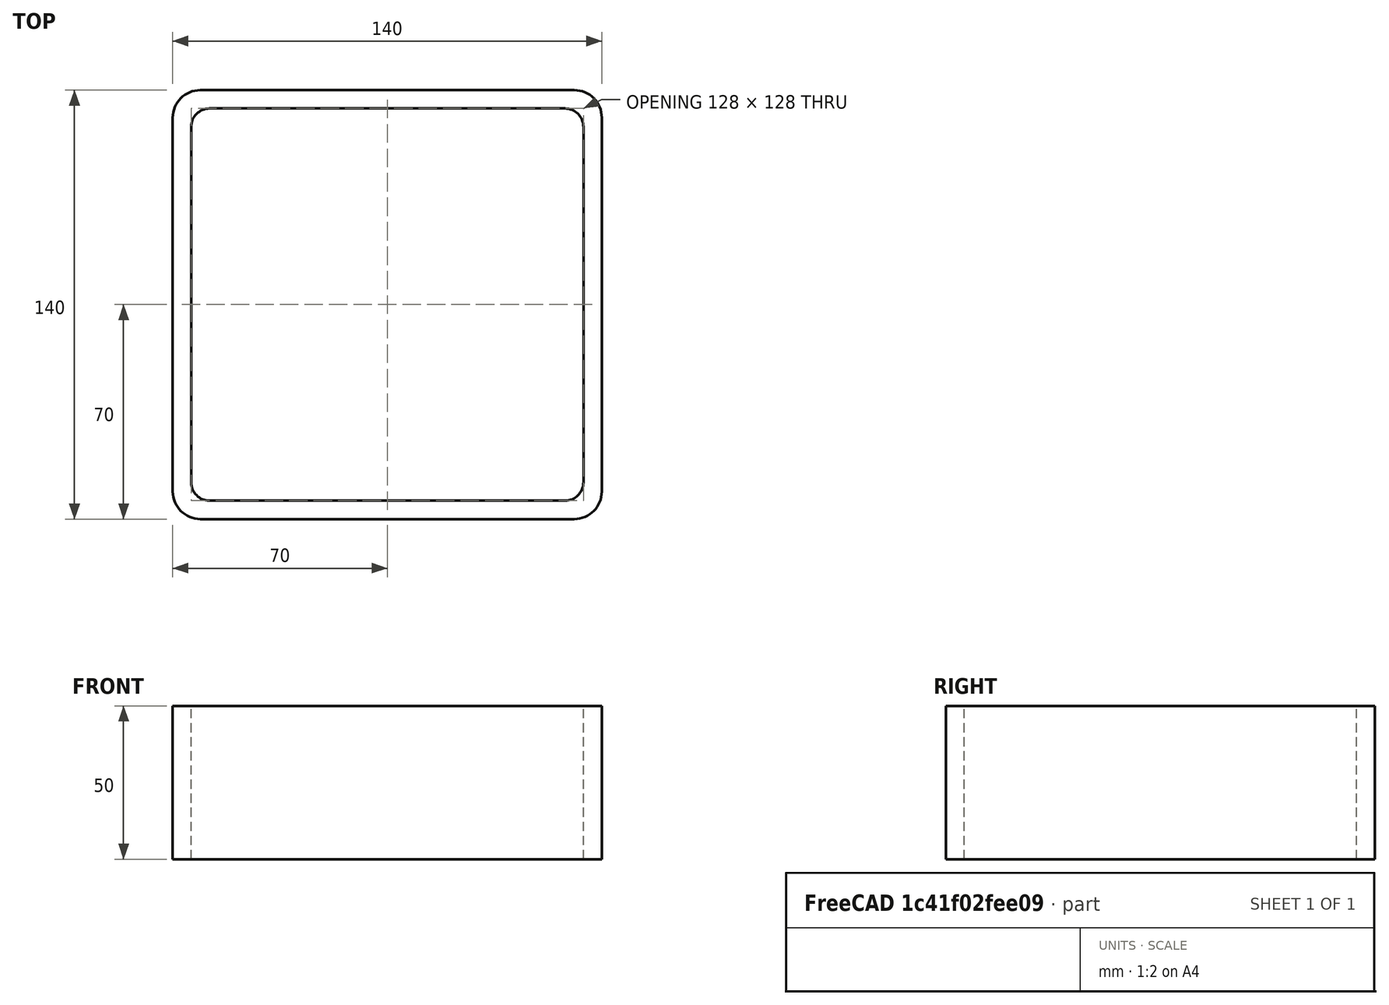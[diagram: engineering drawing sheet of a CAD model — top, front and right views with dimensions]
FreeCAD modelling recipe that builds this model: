
FCSTD DOCUMENT  (FreeCAD 0.15R4671 (Git))
Label: Square hollow section 140x140x6 EN10219 S235JRH
License: All rights reserved
LicenseURL: http://en.wikipedia.org/wiki/All_rights_reserved
objects: Sketcher::SketchObject×1, Part::Extrusion×1
note: 2 computed .brp shape members not serialized (recipe doc carries the construction recipe); baked Part::Feature solids carry a one-line shape summary decoded from their .brp

FEATURE [Sketcher::SketchObject] Sketch
  sketch-geometry (16):
    g0: LineSegment StartX=-58 StartY=64 StartZ=0 EndX=58 EndY=64 EndZ=0
    g1: LineSegment StartX=64 StartY=58 StartZ=0 EndX=64 EndY=-58 EndZ=0
    g2: LineSegment StartX=58 StartY=-64 StartZ=0 EndX=-58 EndY=-64 EndZ=0
    g3: LineSegment StartX=-64 StartY=-58 StartZ=0 EndX=-64 EndY=58 EndZ=0
    g4: LineSegment StartX=-61 StartY=70 StartZ=0 EndX=61 EndY=70 EndZ=0
    g5: LineSegment StartX=70 StartY=61 StartZ=0 EndX=70 EndY=-61 EndZ=0
    g6: LineSegment StartX=61 StartY=-70 StartZ=0 EndX=-61 EndY=-70 EndZ=0
    g7: LineSegment StartX=-70 StartY=-61 StartZ=0 EndX=-70 EndY=61 EndZ=0
    g8: ArcOfCircle CenterX=-58 CenterY=58 CenterZ=0 NormalX=0 NormalY=0 NormalZ=1 Radius=6 StartAngle=1.5708 EndAngle=3.14159
    g9: ArcOfCircle CenterX=58 CenterY=58 CenterZ=0 NormalX=0 NormalY=0 NormalZ=1 Radius=6 StartAngle=0 EndAngle=1.5708
    g10: ArcOfCircle CenterX=58 CenterY=-58 CenterZ=0 NormalX=0 NormalY=0 NormalZ=1 Radius=6 StartAngle=4.71239 EndAngle=6.28319
    g11: ArcOfCircle CenterX=-58 CenterY=-58 CenterZ=0 NormalX=0 NormalY=0 NormalZ=1 Radius=6 StartAngle=3.14159 EndAngle=4.71239
    g12: ArcOfCircle CenterX=61 CenterY=61 CenterZ=0 NormalX=0 NormalY=0 NormalZ=1 Radius=9 StartAngle=0 EndAngle=1.5708
    g13: ArcOfCircle CenterX=61 CenterY=-61 CenterZ=0 NormalX=0 NormalY=0 NormalZ=1 Radius=9 StartAngle=4.71239 EndAngle=6.28319
    g14: ArcOfCircle CenterX=-61 CenterY=-61 CenterZ=0 NormalX=0 NormalY=0 NormalZ=1 Radius=9 StartAngle=3.14159 EndAngle=4.71239
    g15: ArcOfCircle CenterX=-61 CenterY=61 CenterZ=0 NormalX=0 NormalY=0 NormalZ=1 Radius=9 StartAngle=1.5708 EndAngle=3.14159
  constraints (36):
    c: Horizontal(g2)
    c: Vertical(g3)
    c: Horizontal(g6)
    c: Vertical(g7)
    c: Tangent(g3,g8) = 1.5708
    c: Tangent(g0,g8) = 1.5708
    c: Tangent(g0,g9) = 1.5708
    c: Tangent(g1,g9) = 1.5708
    c: Tangent(g1,g10) = 1.5708
    c: Tangent(g2,g10) = 1.5708
    c: Tangent(g2,g11) = 1.5708
    c: Tangent(g3,g11) = 1.5708
    c: Tangent(g4,g12) = 1.5708
    c: Tangent(g5,g12) = 1.5708
    c: Tangent(g5,g13) = 1.5708
    c: Tangent(g6,g13) = 1.5708
    c: Tangent(g6,g14) = 1.5708
    c: Tangent(g7,g14) = 1.5708
    c: Tangent(g7,g15) = 1.5708
    c: Tangent(g4,g15) = 1.5708
    c: Equal(g9,g8)
    c: Equal(g9,g11)
    c: Equal(g9,g10)
    c: Equal(g12,g15)
    c: Equal(g12,g14)
    c: Equal(g12,g13)
    c: Symmetric(g4,g6,g-1)
    c: Symmetric(g7,g5,g-2)
    c: DistanceY(g4,g6) = -140
    c: DistanceX(g7,g5) = 140
    c: Symmetric(g3,g1,g-2)
    c: Symmetric(g0,g2,g-1)
    c: DistanceY(g0,g4) = 6
    c: DistanceX(g5,g1) = -6
    c: Radius(g9) = 6
    c: Radius(g12) = 9
FEATURE [Part::Extrusion] Extrude  label="Square hollow section 140x140x6 EN10219 S235JRH"
  Base = -> Sketch
  Dir = (0,0,50)
  Solid = true
